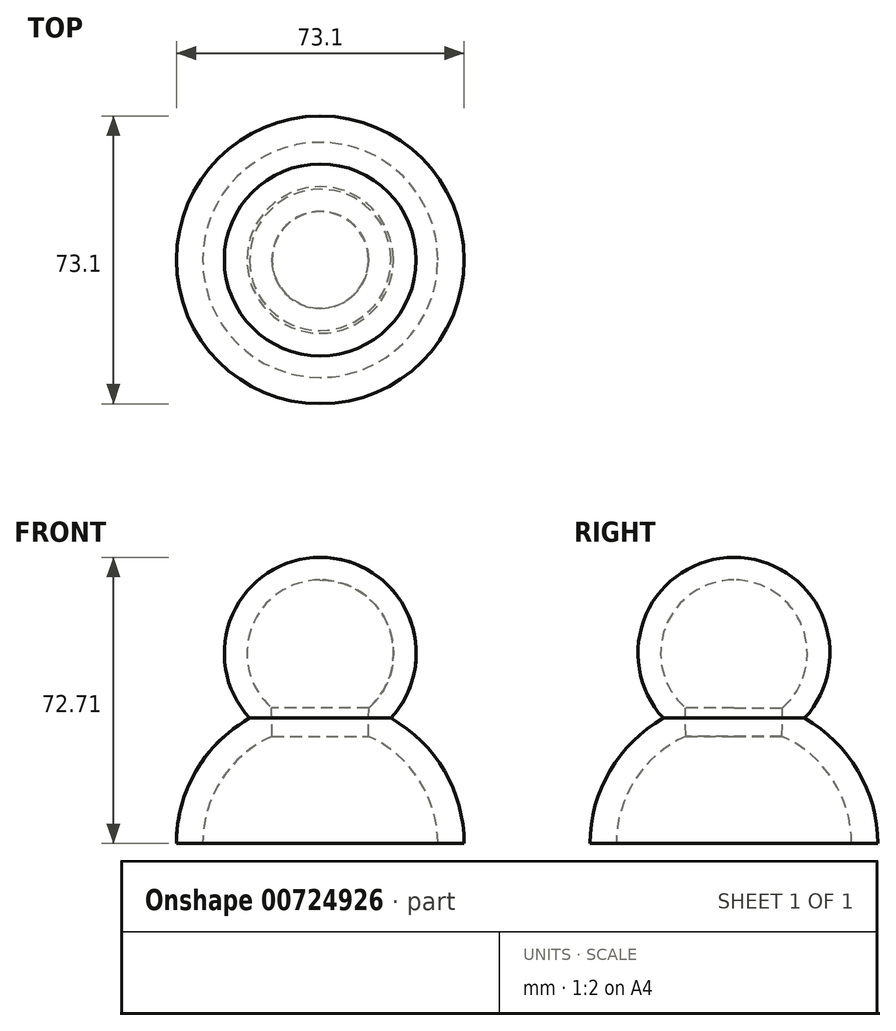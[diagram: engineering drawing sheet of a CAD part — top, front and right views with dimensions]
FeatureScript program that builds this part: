
annotation { "Feature Type Name" : "Feature", "Feature Type Description" : "" }
export const myFeature = defineFeature(function(context is Context, id is Id, definition is map)
    precondition{}
    {
        {
            var Q0;
            Q0=qCreatedBy(makeId("Front.planeOp"),FACE);
            var sketch = newSketch(context, id + "F0", { "sketchPlane" : qUnion([Q0])});
            skArc(sketch, "E0", {"start": v(36.55, 0) * mm, "mid": v(31.56, 18.43) * mm, "end": v(17.95, 31.83) * mm});
            skArc(sketch, "E1", {"start": v(17.95, 31.83) * mm, "mid": v(22.32, 58.13) * mm, "end": v(0, 72.7) * mm});
            skArc(sketch, "E2", {"start": v(29.87, 0) * mm, "mid": v(25.08, 16.23) * mm, "end": v(12.24, 27.25) * mm});
            skLineSegment(sketch, "E3", {"start": v(29.87, 0) * mm, "end": v(36.55, 0) * mm});
            skArc(sketch, "E4.trimOffspring", {"start": v(12.34, 34.4) * mm, "mid": v(17.4, 54.93) * mm, "end": v(0, 66.94) * mm});
            skLineSegment(sketch, "E5", {"start": v(12.34, 34.4) * mm, "end": v(12.24, 27.25) * mm});
            skLineSegment(sketch, "E6.trimOffspring", {"start": v(0, 66.94) * mm, "end": v(0, 72.7) * mm});
            skLineSegment(sketch, "E7", {"start": v(0, 0) * mm, "end": v(0, 48.33) * mm});
            skSolve(sketch);
        }
        {
            var Q0;
            Q0=makeQuery(id+"F0.imprint","IMPRINT",FACE,{"disambiguationData":[TD([[makeQuery(id+"F0.imprint","IMPRINT",EDGE,{"derivedFrom":sQuery(id+"F0.wireOp",EDGE,"E0")}),1.0]])]});
            var Q1;
            Q1=sQuery(id+"F0.wireOp",EDGE,"E7");
            revolve(context, id + "F1", {"surfaceOperationType" : NewSurfaceOperationType.NEW, "entities" : qUnion([Q0]), "axis" : qUnion([Q1]), "revolveType" : RevolveType.FULL});
        }
    });
